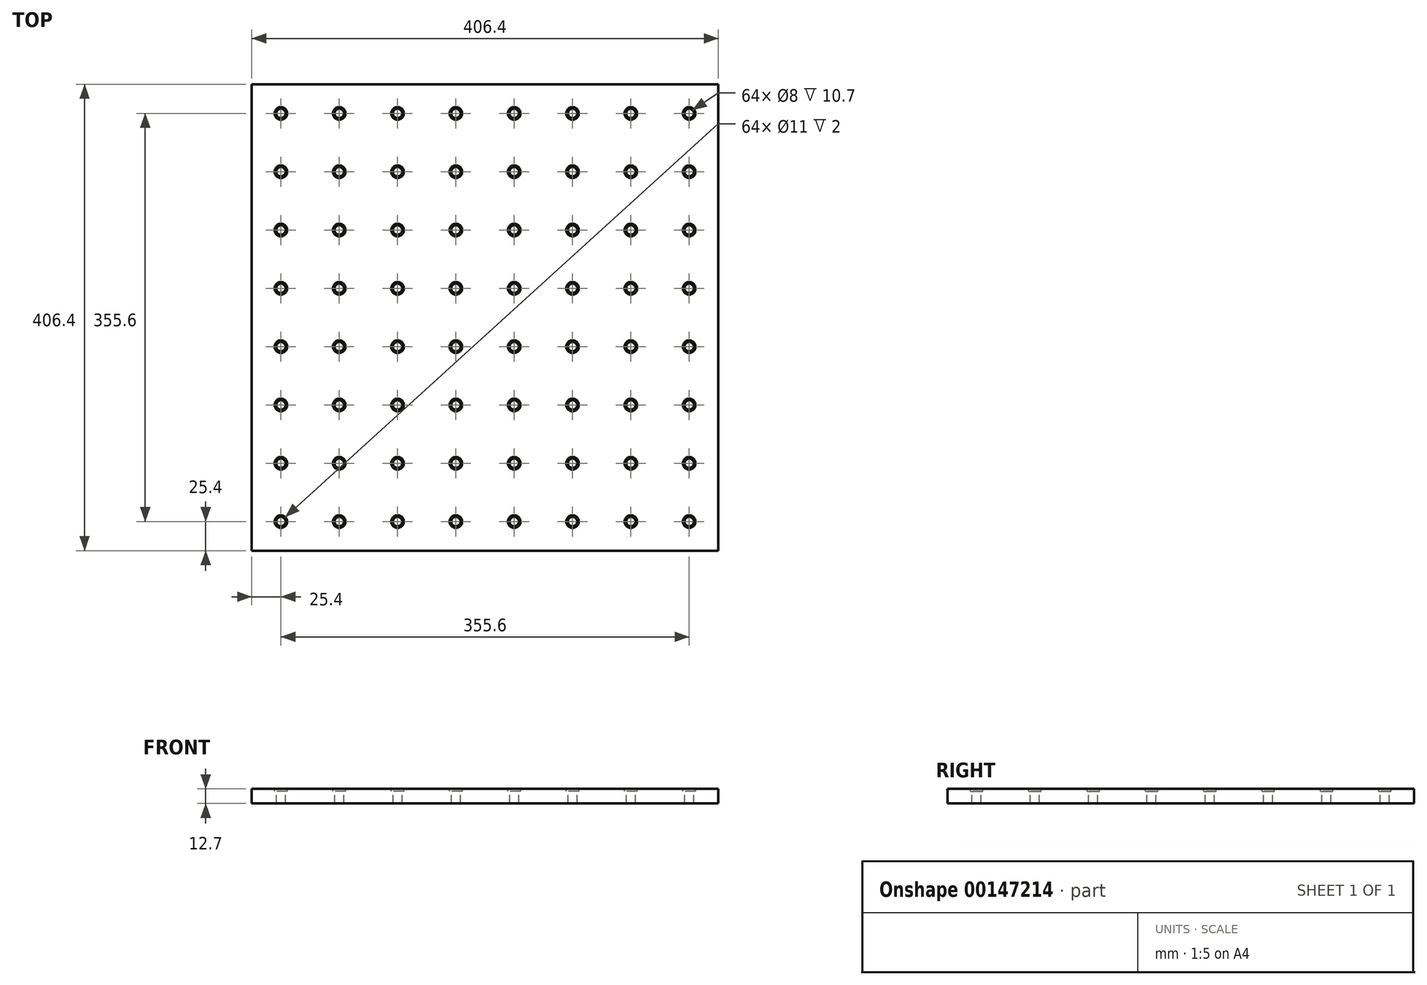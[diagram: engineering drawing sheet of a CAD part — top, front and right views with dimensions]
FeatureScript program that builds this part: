
annotation { "Feature Type Name" : "Feature", "Feature Type Description" : "" }
export const myFeature = defineFeature(function(context is Context, id is Id, definition is map)
    precondition{}
    {
        {
            var Q0;
            Q0=qCreatedBy(makeId("Top.planeOp"),FACE);
            var sketch = newSketch(context, id + "F0", { "sketchPlane" : qUnion([Q0])});
            skLineSegment(sketch, "E0.bottom", {"start": v(0, 0) * mm, "end": v(406.4, 0) * mm});
            skLineSegment(sketch, "E0.top", {"start": v(0, -406.4) * mm, "end": v(406.4, -406.4) * mm});
            skLineSegment(sketch, "E0.left", {"start": v(0, 0) * mm, "end": v(0, -406.4) * mm});
            skLineSegment(sketch, "E0.right", {"start": v(406.4, 0) * mm, "end": v(406.4, -406.4) * mm});
            skLineSegment(sketch, "E1", {"start": v(25.4, 5.4) * mm, "end": v(25.4, -53.58) * mm, "construction": true});
            skLineSegment(sketch, "E2", {"start": v(-10.34, -25.4) * mm, "end": v(59.96, -25.4) * mm, "construction": true});
            skCircle(sketch, "E3", {"center": v(25.4, -25.4) * mm, "radius": 4 * mm});
            skCircle(sketch, "E4", {"center": v(25.4, -25.4) * mm, "radius": 5.5 * mm});
            skCircle(sketch, "E5.0.1.0", {"center": v(25.4, -76.2) * mm, "radius": 5.5 * mm});
            skCircle(sketch, "E5.0.1.1", {"center": v(25.4, -76.2) * mm, "radius": 4 * mm});
            skCircle(sketch, "E5.0.2.0", {"center": v(25.4, -127) * mm, "radius": 5.5 * mm});
            skCircle(sketch, "E5.0.2.1", {"center": v(25.4, -127) * mm, "radius": 4 * mm});
            skCircle(sketch, "E5.0.3.0", {"center": v(25.4, -177.8) * mm, "radius": 5.5 * mm});
            skCircle(sketch, "E5.0.3.1", {"center": v(25.4, -177.8) * mm, "radius": 4 * mm});
            skCircle(sketch, "E5.0.4.0", {"center": v(25.4, -228.6) * mm, "radius": 5.5 * mm});
            skCircle(sketch, "E5.0.4.1", {"center": v(25.4, -228.6) * mm, "radius": 4 * mm});
            skCircle(sketch, "E5.0.5.0", {"center": v(25.4, -279.4) * mm, "radius": 5.5 * mm});
            skCircle(sketch, "E5.0.5.1", {"center": v(25.4, -279.4) * mm, "radius": 4 * mm});
            skCircle(sketch, "E5.0.6.0", {"center": v(25.4, -330.2) * mm, "radius": 5.5 * mm});
            skCircle(sketch, "E5.0.6.1", {"center": v(25.4, -330.2) * mm, "radius": 4 * mm});
            skCircle(sketch, "E5.0.7.0", {"center": v(25.4, -381) * mm, "radius": 5.5 * mm});
            skCircle(sketch, "E5.0.7.1", {"center": v(25.4, -381) * mm, "radius": 4 * mm});
            skCircle(sketch, "E5.1.0.0", {"center": v(76.2, -25.4) * mm, "radius": 5.5 * mm});
            skCircle(sketch, "E5.1.0.1", {"center": v(76.2, -25.4) * mm, "radius": 4 * mm});
            skCircle(sketch, "E5.1.1.0", {"center": v(76.2, -76.2) * mm, "radius": 5.5 * mm});
            skCircle(sketch, "E5.1.1.1", {"center": v(76.2, -76.2) * mm, "radius": 4 * mm});
            skCircle(sketch, "E5.1.2.0", {"center": v(76.2, -127) * mm, "radius": 5.5 * mm});
            skCircle(sketch, "E5.1.2.1", {"center": v(76.2, -127) * mm, "radius": 4 * mm});
            skCircle(sketch, "E5.1.3.0", {"center": v(76.2, -177.8) * mm, "radius": 5.5 * mm});
            skCircle(sketch, "E5.1.3.1", {"center": v(76.2, -177.8) * mm, "radius": 4 * mm});
            skCircle(sketch, "E5.1.4.0", {"center": v(76.2, -228.6) * mm, "radius": 5.5 * mm});
            skCircle(sketch, "E5.1.4.1", {"center": v(76.2, -228.6) * mm, "radius": 4 * mm});
            skCircle(sketch, "E5.1.5.0", {"center": v(76.2, -279.4) * mm, "radius": 5.5 * mm});
            skCircle(sketch, "E5.1.5.1", {"center": v(76.2, -279.4) * mm, "radius": 4 * mm});
            skCircle(sketch, "E5.1.6.0", {"center": v(76.2, -330.2) * mm, "radius": 5.5 * mm});
            skCircle(sketch, "E5.1.6.1", {"center": v(76.2, -330.2) * mm, "radius": 4 * mm});
            skCircle(sketch, "E5.1.7.0", {"center": v(76.2, -381) * mm, "radius": 5.5 * mm});
            skCircle(sketch, "E5.1.7.1", {"center": v(76.2, -381) * mm, "radius": 4 * mm});
            skCircle(sketch, "E5.2.0.0", {"center": v(127, -25.4) * mm, "radius": 5.5 * mm});
            skCircle(sketch, "E5.2.0.1", {"center": v(127, -25.4) * mm, "radius": 4 * mm});
            skCircle(sketch, "E5.2.1.0", {"center": v(127, -76.2) * mm, "radius": 5.5 * mm});
            skCircle(sketch, "E5.2.1.1", {"center": v(127, -76.2) * mm, "radius": 4 * mm});
            skCircle(sketch, "E5.2.2.0", {"center": v(127, -127) * mm, "radius": 5.5 * mm});
            skCircle(sketch, "E5.2.2.1", {"center": v(127, -127) * mm, "radius": 4 * mm});
            skCircle(sketch, "E5.2.3.0", {"center": v(127, -177.8) * mm, "radius": 5.5 * mm});
            skCircle(sketch, "E5.2.3.1", {"center": v(127, -177.8) * mm, "radius": 4 * mm});
            skCircle(sketch, "E5.2.4.0", {"center": v(127, -228.6) * mm, "radius": 5.5 * mm});
            skCircle(sketch, "E5.2.4.1", {"center": v(127, -228.6) * mm, "radius": 4 * mm});
            skCircle(sketch, "E5.2.5.0", {"center": v(127, -279.4) * mm, "radius": 5.5 * mm});
            skCircle(sketch, "E5.2.5.1", {"center": v(127, -279.4) * mm, "radius": 4 * mm});
            skCircle(sketch, "E5.2.6.0", {"center": v(127, -330.2) * mm, "radius": 5.5 * mm});
            skCircle(sketch, "E5.2.6.1", {"center": v(127, -330.2) * mm, "radius": 4 * mm});
            skCircle(sketch, "E5.2.7.0", {"center": v(127, -381) * mm, "radius": 5.5 * mm});
            skCircle(sketch, "E5.2.7.1", {"center": v(127, -381) * mm, "radius": 4 * mm});
            skCircle(sketch, "E5.3.0.0", {"center": v(177.8, -25.4) * mm, "radius": 5.5 * mm});
            skCircle(sketch, "E5.3.0.1", {"center": v(177.8, -25.4) * mm, "radius": 4 * mm});
            skCircle(sketch, "E5.3.1.0", {"center": v(177.8, -76.2) * mm, "radius": 5.5 * mm});
            skCircle(sketch, "E5.3.1.1", {"center": v(177.8, -76.2) * mm, "radius": 4 * mm});
            skCircle(sketch, "E5.3.2.0", {"center": v(177.8, -127) * mm, "radius": 5.5 * mm});
            skCircle(sketch, "E5.3.2.1", {"center": v(177.8, -127) * mm, "radius": 4 * mm});
            skCircle(sketch, "E5.3.3.0", {"center": v(177.8, -177.8) * mm, "radius": 5.5 * mm});
            skCircle(sketch, "E5.3.3.1", {"center": v(177.8, -177.8) * mm, "radius": 4 * mm});
            skCircle(sketch, "E5.3.4.0", {"center": v(177.8, -228.6) * mm, "radius": 5.5 * mm});
            skCircle(sketch, "E5.3.4.1", {"center": v(177.8, -228.6) * mm, "radius": 4 * mm});
            skCircle(sketch, "E5.3.5.0", {"center": v(177.8, -279.4) * mm, "radius": 5.5 * mm});
            skCircle(sketch, "E5.3.5.1", {"center": v(177.8, -279.4) * mm, "radius": 4 * mm});
            skCircle(sketch, "E5.3.6.0", {"center": v(177.8, -330.2) * mm, "radius": 5.5 * mm});
            skCircle(sketch, "E5.3.6.1", {"center": v(177.8, -330.2) * mm, "radius": 4 * mm});
            skCircle(sketch, "E5.3.7.0", {"center": v(177.8, -381) * mm, "radius": 5.5 * mm});
            skCircle(sketch, "E5.3.7.1", {"center": v(177.8, -381) * mm, "radius": 4 * mm});
            skCircle(sketch, "E5.4.0.0", {"center": v(228.6, -25.4) * mm, "radius": 5.5 * mm});
            skCircle(sketch, "E5.4.0.1", {"center": v(228.6, -25.4) * mm, "radius": 4 * mm});
            skCircle(sketch, "E5.4.1.0", {"center": v(228.6, -76.2) * mm, "radius": 5.5 * mm});
            skCircle(sketch, "E5.4.1.1", {"center": v(228.6, -76.2) * mm, "radius": 4 * mm});
            skCircle(sketch, "E5.4.2.0", {"center": v(228.6, -127) * mm, "radius": 5.5 * mm});
            skCircle(sketch, "E5.4.2.1", {"center": v(228.6, -127) * mm, "radius": 4 * mm});
            skCircle(sketch, "E5.4.3.0", {"center": v(228.6, -177.8) * mm, "radius": 5.5 * mm});
            skCircle(sketch, "E5.4.3.1", {"center": v(228.6, -177.8) * mm, "radius": 4 * mm});
            skCircle(sketch, "E5.4.4.0", {"center": v(228.6, -228.6) * mm, "radius": 5.5 * mm});
            skCircle(sketch, "E5.4.4.1", {"center": v(228.6, -228.6) * mm, "radius": 4 * mm});
            skCircle(sketch, "E5.4.5.0", {"center": v(228.6, -279.4) * mm, "radius": 5.5 * mm});
            skCircle(sketch, "E5.4.5.1", {"center": v(228.6, -279.4) * mm, "radius": 4 * mm});
            skCircle(sketch, "E5.4.6.0", {"center": v(228.6, -330.2) * mm, "radius": 5.5 * mm});
            skCircle(sketch, "E5.4.6.1", {"center": v(228.6, -330.2) * mm, "radius": 4 * mm});
            skCircle(sketch, "E5.4.7.0", {"center": v(228.6, -381) * mm, "radius": 5.5 * mm});
            skCircle(sketch, "E5.4.7.1", {"center": v(228.6, -381) * mm, "radius": 4 * mm});
            skCircle(sketch, "E5.5.0.0", {"center": v(279.4, -25.4) * mm, "radius": 5.5 * mm});
            skCircle(sketch, "E5.5.0.1", {"center": v(279.4, -25.4) * mm, "radius": 4 * mm});
            skCircle(sketch, "E5.5.1.0", {"center": v(279.4, -76.2) * mm, "radius": 5.5 * mm});
            skCircle(sketch, "E5.5.1.1", {"center": v(279.4, -76.2) * mm, "radius": 4 * mm});
            skCircle(sketch, "E5.5.2.0", {"center": v(279.4, -127) * mm, "radius": 5.5 * mm});
            skCircle(sketch, "E5.5.2.1", {"center": v(279.4, -127) * mm, "radius": 4 * mm});
            skCircle(sketch, "E5.5.3.0", {"center": v(279.4, -177.8) * mm, "radius": 5.5 * mm});
            skCircle(sketch, "E5.5.3.1", {"center": v(279.4, -177.8) * mm, "radius": 4 * mm});
            skCircle(sketch, "E5.5.4.0", {"center": v(279.4, -228.6) * mm, "radius": 5.5 * mm});
            skCircle(sketch, "E5.5.4.1", {"center": v(279.4, -228.6) * mm, "radius": 4 * mm});
            skCircle(sketch, "E5.5.5.0", {"center": v(279.4, -279.4) * mm, "radius": 5.5 * mm});
            skCircle(sketch, "E5.5.5.1", {"center": v(279.4, -279.4) * mm, "radius": 4 * mm});
            skCircle(sketch, "E5.5.6.0", {"center": v(279.4, -330.2) * mm, "radius": 5.5 * mm});
            skCircle(sketch, "E5.5.6.1", {"center": v(279.4, -330.2) * mm, "radius": 4 * mm});
            skCircle(sketch, "E5.5.7.0", {"center": v(279.4, -381) * mm, "radius": 5.5 * mm});
            skCircle(sketch, "E5.5.7.1", {"center": v(279.4, -381) * mm, "radius": 4 * mm});
            skCircle(sketch, "E5.6.0.0", {"center": v(330.2, -25.4) * mm, "radius": 5.5 * mm});
            skCircle(sketch, "E5.6.0.1", {"center": v(330.2, -25.4) * mm, "radius": 4 * mm});
            skCircle(sketch, "E5.6.1.0", {"center": v(330.2, -76.2) * mm, "radius": 5.5 * mm});
            skCircle(sketch, "E5.6.1.1", {"center": v(330.2, -76.2) * mm, "radius": 4 * mm});
            skCircle(sketch, "E5.6.2.0", {"center": v(330.2, -127) * mm, "radius": 5.5 * mm});
            skCircle(sketch, "E5.6.2.1", {"center": v(330.2, -127) * mm, "radius": 4 * mm});
            skCircle(sketch, "E5.6.3.0", {"center": v(330.2, -177.8) * mm, "radius": 5.5 * mm});
            skCircle(sketch, "E5.6.3.1", {"center": v(330.2, -177.8) * mm, "radius": 4 * mm});
            skCircle(sketch, "E5.6.4.0", {"center": v(330.2, -228.6) * mm, "radius": 5.5 * mm});
            skCircle(sketch, "E5.6.4.1", {"center": v(330.2, -228.6) * mm, "radius": 4 * mm});
            skCircle(sketch, "E5.6.5.0", {"center": v(330.2, -279.4) * mm, "radius": 5.5 * mm});
            skCircle(sketch, "E5.6.5.1", {"center": v(330.2, -279.4) * mm, "radius": 4 * mm});
            skCircle(sketch, "E5.6.6.0", {"center": v(330.2, -330.2) * mm, "radius": 5.5 * mm});
            skCircle(sketch, "E5.6.6.1", {"center": v(330.2, -330.2) * mm, "radius": 4 * mm});
            skCircle(sketch, "E5.6.7.0", {"center": v(330.2, -381) * mm, "radius": 5.5 * mm});
            skCircle(sketch, "E5.6.7.1", {"center": v(330.2, -381) * mm, "radius": 4 * mm});
            skCircle(sketch, "E5.7.0.0", {"center": v(381, -25.4) * mm, "radius": 5.5 * mm});
            skCircle(sketch, "E5.7.0.1", {"center": v(381, -25.4) * mm, "radius": 4 * mm});
            skCircle(sketch, "E5.7.1.0", {"center": v(381, -76.2) * mm, "radius": 5.5 * mm});
            skCircle(sketch, "E5.7.1.1", {"center": v(381, -76.2) * mm, "radius": 4 * mm});
            skCircle(sketch, "E5.7.2.0", {"center": v(381, -127) * mm, "radius": 5.5 * mm});
            skCircle(sketch, "E5.7.2.1", {"center": v(381, -127) * mm, "radius": 4 * mm});
            skCircle(sketch, "E5.7.3.0", {"center": v(381, -177.8) * mm, "radius": 5.5 * mm});
            skCircle(sketch, "E5.7.3.1", {"center": v(381, -177.8) * mm, "radius": 4 * mm});
            skCircle(sketch, "E5.7.4.0", {"center": v(381, -228.6) * mm, "radius": 5.5 * mm});
            skCircle(sketch, "E5.7.4.1", {"center": v(381, -228.6) * mm, "radius": 4 * mm});
            skCircle(sketch, "E5.7.5.0", {"center": v(381, -279.4) * mm, "radius": 5.5 * mm});
            skCircle(sketch, "E5.7.5.1", {"center": v(381, -279.4) * mm, "radius": 4 * mm});
            skCircle(sketch, "E5.7.6.0", {"center": v(381, -330.2) * mm, "radius": 5.5 * mm});
            skCircle(sketch, "E5.7.6.1", {"center": v(381, -330.2) * mm, "radius": 4 * mm});
            skCircle(sketch, "E5.7.7.0", {"center": v(381, -381) * mm, "radius": 5.5 * mm});
            skCircle(sketch, "E5.7.7.1", {"center": v(381, -381) * mm, "radius": 4 * mm});
            skLineSegment(sketch, "E5.direction1", {"start": v(25.4, -25.4) * mm, "end": v(76.2, -25.4) * mm, "construction": true});
            skLineSegment(sketch, "E5.direction2", {"start": v(25.4, -25.4) * mm, "end": v(25.4, -76.2) * mm, "construction": true});
            skSolve(sketch);
        }
        {
            var Q0;
            Q0 = qSketchRegion(id + "F0", true);
            var Q1;
            Q1=makeQuery(id+"F0.imprint","IMPRINT",FACE,{"disambiguationData":[TD([[makeQuery(id+"F0.imprint","IMPRINT",EDGE,{"derivedFrom":sQuery(id+"F0.wireOp",EDGE,"E3")}),-1.0]])]});
            var Q2;
            Q2=makeQuery(id+"F0.imprint","IMPRINT",FACE,{"disambiguationData":[TD([[makeQuery(id+"F0.imprint","IMPRINT",EDGE,{"derivedFrom":sQuery(id+"F0.wireOp",EDGE,"E5.1.0.0")}),1.0]])]});
            var Q3;
            Q3=makeQuery(id+"F0.imprint","IMPRINT",FACE,{"disambiguationData":[TD([[makeQuery(id+"F0.imprint","IMPRINT",EDGE,{"derivedFrom":sQuery(id+"F0.wireOp",EDGE,"E5.2.0.0")}),1.0]])]});
            var Q4;
            Q4=makeQuery(id+"F0.imprint","IMPRINT",FACE,{"disambiguationData":[TD([[makeQuery(id+"F0.imprint","IMPRINT",EDGE,{"derivedFrom":sQuery(id+"F0.wireOp",EDGE,"E5.3.0.0")}),1.0]])]});
            var Q5;
            Q5=makeQuery(id+"F0.imprint","IMPRINT",FACE,{"disambiguationData":[TD([[makeQuery(id+"F0.imprint","IMPRINT",EDGE,{"derivedFrom":sQuery(id+"F0.wireOp",EDGE,"E5.4.0.0")}),1.0]])]});
            var Q6;
            Q6=makeQuery(id+"F0.imprint","IMPRINT",FACE,{"disambiguationData":[TD([[makeQuery(id+"F0.imprint","IMPRINT",EDGE,{"derivedFrom":sQuery(id+"F0.wireOp",EDGE,"E5.5.0.0")}),1.0]])]});
            var Q7;
            Q7=makeQuery(id+"F0.imprint","IMPRINT",FACE,{"disambiguationData":[TD([[makeQuery(id+"F0.imprint","IMPRINT",EDGE,{"derivedFrom":sQuery(id+"F0.wireOp",EDGE,"E5.6.0.0")}),1.0]])]});
            var Q8;
            Q8=makeQuery(id+"F0.imprint","IMPRINT",FACE,{"disambiguationData":[TD([[makeQuery(id+"F0.imprint","IMPRINT",EDGE,{"derivedFrom":sQuery(id+"F0.wireOp",EDGE,"E5.7.0.0")}),1.0]])]});
            var Q9;
            Q9=makeQuery(id+"F0.imprint","IMPRINT",FACE,{"disambiguationData":[TD([[makeQuery(id+"F0.imprint","IMPRINT",EDGE,{"derivedFrom":sQuery(id+"F0.wireOp",EDGE,"E5.0.1.0")}),1.0]])]});
            var Q10;
            Q10=makeQuery(id+"F0.imprint","IMPRINT",FACE,{"disambiguationData":[TD([[makeQuery(id+"F0.imprint","IMPRINT",EDGE,{"derivedFrom":sQuery(id+"F0.wireOp",EDGE,"E5.1.1.0")}),1.0]])]});
            var Q11;
            Q11=makeQuery(id+"F0.imprint","IMPRINT",FACE,{"disambiguationData":[TD([[makeQuery(id+"F0.imprint","IMPRINT",EDGE,{"derivedFrom":sQuery(id+"F0.wireOp",EDGE,"E5.2.1.0")}),1.0]])]});
            var Q12;
            Q12=makeQuery(id+"F0.imprint","IMPRINT",FACE,{"disambiguationData":[TD([[makeQuery(id+"F0.imprint","IMPRINT",EDGE,{"derivedFrom":sQuery(id+"F0.wireOp",EDGE,"E5.3.1.0")}),1.0]])]});
            var Q13;
            Q13=makeQuery(id+"F0.imprint","IMPRINT",FACE,{"disambiguationData":[TD([[makeQuery(id+"F0.imprint","IMPRINT",EDGE,{"derivedFrom":sQuery(id+"F0.wireOp",EDGE,"E5.4.1.0")}),1.0]])]});
            var Q14;
            Q14=makeQuery(id+"F0.imprint","IMPRINT",FACE,{"disambiguationData":[TD([[makeQuery(id+"F0.imprint","IMPRINT",EDGE,{"derivedFrom":sQuery(id+"F0.wireOp",EDGE,"E5.5.1.0")}),1.0]])]});
            var Q15;
            Q15=makeQuery(id+"F0.imprint","IMPRINT",FACE,{"disambiguationData":[TD([[makeQuery(id+"F0.imprint","IMPRINT",EDGE,{"derivedFrom":sQuery(id+"F0.wireOp",EDGE,"E5.6.1.0")}),1.0]])]});
            var Q16;
            Q16=makeQuery(id+"F0.imprint","IMPRINT",FACE,{"disambiguationData":[TD([[makeQuery(id+"F0.imprint","IMPRINT",EDGE,{"derivedFrom":sQuery(id+"F0.wireOp",EDGE,"E5.7.1.0")}),1.0]])]});
            var Q17;
            Q17=makeQuery(id+"F0.imprint","IMPRINT",FACE,{"disambiguationData":[TD([[makeQuery(id+"F0.imprint","IMPRINT",EDGE,{"derivedFrom":sQuery(id+"F0.wireOp",EDGE,"E5.7.2.0")}),1.0]])]});
            var Q18;
            Q18=makeQuery(id+"F0.imprint","IMPRINT",FACE,{"disambiguationData":[TD([[makeQuery(id+"F0.imprint","IMPRINT",EDGE,{"derivedFrom":sQuery(id+"F0.wireOp",EDGE,"E5.6.2.0")}),1.0]])]});
            var Q19;
            Q19=makeQuery(id+"F0.imprint","IMPRINT",FACE,{"disambiguationData":[TD([[makeQuery(id+"F0.imprint","IMPRINT",EDGE,{"derivedFrom":sQuery(id+"F0.wireOp",EDGE,"E5.5.2.0")}),1.0]])]});
            var Q20;
            Q20=makeQuery(id+"F0.imprint","IMPRINT",FACE,{"disambiguationData":[TD([[makeQuery(id+"F0.imprint","IMPRINT",EDGE,{"derivedFrom":sQuery(id+"F0.wireOp",EDGE,"E5.4.2.0")}),1.0]])]});
            var Q21;
            Q21=makeQuery(id+"F0.imprint","IMPRINT",FACE,{"disambiguationData":[TD([[makeQuery(id+"F0.imprint","IMPRINT",EDGE,{"derivedFrom":sQuery(id+"F0.wireOp",EDGE,"E5.3.2.0")}),1.0]])]});
            var Q22;
            Q22=makeQuery(id+"F0.imprint","IMPRINT",FACE,{"disambiguationData":[TD([[makeQuery(id+"F0.imprint","IMPRINT",EDGE,{"derivedFrom":sQuery(id+"F0.wireOp",EDGE,"E5.2.2.0")}),1.0]])]});
            var Q23;
            Q23=makeQuery(id+"F0.imprint","IMPRINT",FACE,{"disambiguationData":[TD([[makeQuery(id+"F0.imprint","IMPRINT",EDGE,{"derivedFrom":sQuery(id+"F0.wireOp",EDGE,"E5.1.2.0")}),1.0]])]});
            var Q24;
            Q24=makeQuery(id+"F0.imprint","IMPRINT",FACE,{"disambiguationData":[TD([[makeQuery(id+"F0.imprint","IMPRINT",EDGE,{"derivedFrom":sQuery(id+"F0.wireOp",EDGE,"E5.0.2.0")}),1.0]])]});
            var Q25;
            Q25=makeQuery(id+"F0.imprint","IMPRINT",FACE,{"disambiguationData":[TD([[makeQuery(id+"F0.imprint","IMPRINT",EDGE,{"derivedFrom":sQuery(id+"F0.wireOp",EDGE,"E5.0.3.0")}),1.0]])]});
            var Q26;
            Q26=makeQuery(id+"F0.imprint","IMPRINT",FACE,{"disambiguationData":[TD([[makeQuery(id+"F0.imprint","IMPRINT",EDGE,{"derivedFrom":sQuery(id+"F0.wireOp",EDGE,"E5.1.3.0")}),1.0]])]});
            var Q27;
            Q27=makeQuery(id+"F0.imprint","IMPRINT",FACE,{"disambiguationData":[TD([[makeQuery(id+"F0.imprint","IMPRINT",EDGE,{"derivedFrom":sQuery(id+"F0.wireOp",EDGE,"E5.2.3.0")}),1.0]])]});
            var Q28;
            Q28=makeQuery(id+"F0.imprint","IMPRINT",FACE,{"disambiguationData":[TD([[makeQuery(id+"F0.imprint","IMPRINT",EDGE,{"derivedFrom":sQuery(id+"F0.wireOp",EDGE,"E5.3.3.0")}),1.0]])]});
            var Q29;
            Q29=makeQuery(id+"F0.imprint","IMPRINT",FACE,{"disambiguationData":[TD([[makeQuery(id+"F0.imprint","IMPRINT",EDGE,{"derivedFrom":sQuery(id+"F0.wireOp",EDGE,"E5.4.3.0")}),1.0]])]});
            var Q30;
            Q30=makeQuery(id+"F0.imprint","IMPRINT",FACE,{"disambiguationData":[TD([[makeQuery(id+"F0.imprint","IMPRINT",EDGE,{"derivedFrom":sQuery(id+"F0.wireOp",EDGE,"E5.5.3.0")}),1.0]])]});
            var Q31;
            Q31=makeQuery(id+"F0.imprint","IMPRINT",FACE,{"disambiguationData":[TD([[makeQuery(id+"F0.imprint","IMPRINT",EDGE,{"derivedFrom":sQuery(id+"F0.wireOp",EDGE,"E5.6.3.0")}),1.0]])]});
            var Q32;
            Q32=makeQuery(id+"F0.imprint","IMPRINT",FACE,{"disambiguationData":[TD([[makeQuery(id+"F0.imprint","IMPRINT",EDGE,{"derivedFrom":sQuery(id+"F0.wireOp",EDGE,"E5.7.3.0")}),1.0]])]});
            var Q33;
            Q33=makeQuery(id+"F0.imprint","IMPRINT",FACE,{"disambiguationData":[TD([[makeQuery(id+"F0.imprint","IMPRINT",EDGE,{"derivedFrom":sQuery(id+"F0.wireOp",EDGE,"E5.7.4.0")}),1.0]])]});
            var Q34;
            Q34=makeQuery(id+"F0.imprint","IMPRINT",FACE,{"disambiguationData":[TD([[makeQuery(id+"F0.imprint","IMPRINT",EDGE,{"derivedFrom":sQuery(id+"F0.wireOp",EDGE,"E5.6.4.0")}),1.0]])]});
            var Q35;
            Q35=makeQuery(id+"F0.imprint","IMPRINT",FACE,{"disambiguationData":[TD([[makeQuery(id+"F0.imprint","IMPRINT",EDGE,{"derivedFrom":sQuery(id+"F0.wireOp",EDGE,"E5.5.4.0")}),1.0]])]});
            var Q36;
            Q36=makeQuery(id+"F0.imprint","IMPRINT",FACE,{"disambiguationData":[TD([[makeQuery(id+"F0.imprint","IMPRINT",EDGE,{"derivedFrom":sQuery(id+"F0.wireOp",EDGE,"E5.4.4.0")}),1.0]])]});
            var Q37;
            Q37=makeQuery(id+"F0.imprint","IMPRINT",FACE,{"disambiguationData":[TD([[makeQuery(id+"F0.imprint","IMPRINT",EDGE,{"derivedFrom":sQuery(id+"F0.wireOp",EDGE,"E5.3.4.0")}),1.0]])]});
            var Q38;
            Q38=makeQuery(id+"F0.imprint","IMPRINT",FACE,{"disambiguationData":[TD([[makeQuery(id+"F0.imprint","IMPRINT",EDGE,{"derivedFrom":sQuery(id+"F0.wireOp",EDGE,"E5.2.4.0")}),1.0]])]});
            var Q39;
            Q39=makeQuery(id+"F0.imprint","IMPRINT",FACE,{"disambiguationData":[TD([[makeQuery(id+"F0.imprint","IMPRINT",EDGE,{"derivedFrom":sQuery(id+"F0.wireOp",EDGE,"E5.1.4.0")}),1.0]])]});
            var Q40;
            Q40=makeQuery(id+"F0.imprint","IMPRINT",FACE,{"disambiguationData":[TD([[makeQuery(id+"F0.imprint","IMPRINT",EDGE,{"derivedFrom":sQuery(id+"F0.wireOp",EDGE,"E5.0.4.0")}),1.0]])]});
            var Q41;
            Q41=makeQuery(id+"F0.imprint","IMPRINT",FACE,{"disambiguationData":[TD([[makeQuery(id+"F0.imprint","IMPRINT",EDGE,{"derivedFrom":sQuery(id+"F0.wireOp",EDGE,"E5.0.5.0")}),1.0]])]});
            var Q42;
            Q42=makeQuery(id+"F0.imprint","IMPRINT",FACE,{"disambiguationData":[TD([[makeQuery(id+"F0.imprint","IMPRINT",EDGE,{"derivedFrom":sQuery(id+"F0.wireOp",EDGE,"E5.1.5.0")}),1.0]])]});
            var Q43;
            Q43=makeQuery(id+"F0.imprint","IMPRINT",FACE,{"disambiguationData":[TD([[makeQuery(id+"F0.imprint","IMPRINT",EDGE,{"derivedFrom":sQuery(id+"F0.wireOp",EDGE,"E5.2.5.0")}),1.0]])]});
            var Q44;
            Q44=makeQuery(id+"F0.imprint","IMPRINT",FACE,{"disambiguationData":[TD([[makeQuery(id+"F0.imprint","IMPRINT",EDGE,{"derivedFrom":sQuery(id+"F0.wireOp",EDGE,"E5.3.5.0")}),1.0]])]});
            var Q45;
            Q45=makeQuery(id+"F0.imprint","IMPRINT",FACE,{"disambiguationData":[TD([[makeQuery(id+"F0.imprint","IMPRINT",EDGE,{"derivedFrom":sQuery(id+"F0.wireOp",EDGE,"E5.4.5.0")}),1.0]])]});
            var Q46;
            Q46=makeQuery(id+"F0.imprint","IMPRINT",FACE,{"disambiguationData":[TD([[makeQuery(id+"F0.imprint","IMPRINT",EDGE,{"derivedFrom":sQuery(id+"F0.wireOp",EDGE,"E5.5.5.0")}),1.0]])]});
            var Q47;
            Q47=makeQuery(id+"F0.imprint","IMPRINT",FACE,{"disambiguationData":[TD([[makeQuery(id+"F0.imprint","IMPRINT",EDGE,{"derivedFrom":sQuery(id+"F0.wireOp",EDGE,"E5.6.5.0")}),1.0]])]});
            var Q48;
            Q48=makeQuery(id+"F0.imprint","IMPRINT",FACE,{"disambiguationData":[TD([[makeQuery(id+"F0.imprint","IMPRINT",EDGE,{"derivedFrom":sQuery(id+"F0.wireOp",EDGE,"E5.7.5.0")}),1.0]])]});
            var Q49;
            Q49=makeQuery(id+"F0.imprint","IMPRINT",FACE,{"disambiguationData":[TD([[makeQuery(id+"F0.imprint","IMPRINT",EDGE,{"derivedFrom":sQuery(id+"F0.wireOp",EDGE,"E5.7.6.0")}),1.0]])]});
            var Q50;
            Q50=makeQuery(id+"F0.imprint","IMPRINT",FACE,{"disambiguationData":[TD([[makeQuery(id+"F0.imprint","IMPRINT",EDGE,{"derivedFrom":sQuery(id+"F0.wireOp",EDGE,"E5.6.6.0")}),1.0]])]});
            var Q51;
            Q51=makeQuery(id+"F0.imprint","IMPRINT",FACE,{"disambiguationData":[TD([[makeQuery(id+"F0.imprint","IMPRINT",EDGE,{"derivedFrom":sQuery(id+"F0.wireOp",EDGE,"E5.5.6.0")}),1.0]])]});
            var Q52;
            Q52=makeQuery(id+"F0.imprint","IMPRINT",FACE,{"disambiguationData":[TD([[makeQuery(id+"F0.imprint","IMPRINT",EDGE,{"derivedFrom":sQuery(id+"F0.wireOp",EDGE,"E5.4.6.0")}),1.0]])]});
            var Q53;
            Q53=makeQuery(id+"F0.imprint","IMPRINT",FACE,{"disambiguationData":[TD([[makeQuery(id+"F0.imprint","IMPRINT",EDGE,{"derivedFrom":sQuery(id+"F0.wireOp",EDGE,"E5.3.6.0")}),1.0]])]});
            var Q54;
            Q54=makeQuery(id+"F0.imprint","IMPRINT",FACE,{"disambiguationData":[TD([[makeQuery(id+"F0.imprint","IMPRINT",EDGE,{"derivedFrom":sQuery(id+"F0.wireOp",EDGE,"E5.2.6.0")}),1.0]])]});
            var Q55;
            Q55=makeQuery(id+"F0.imprint","IMPRINT",FACE,{"disambiguationData":[TD([[makeQuery(id+"F0.imprint","IMPRINT",EDGE,{"derivedFrom":sQuery(id+"F0.wireOp",EDGE,"E5.1.6.0")}),1.0]])]});
            var Q56;
            Q56=makeQuery(id+"F0.imprint","IMPRINT",FACE,{"disambiguationData":[TD([[makeQuery(id+"F0.imprint","IMPRINT",EDGE,{"derivedFrom":sQuery(id+"F0.wireOp",EDGE,"E5.0.6.0")}),1.0]])]});
            var Q57;
            Q57=makeQuery(id+"F0.imprint","IMPRINT",FACE,{"disambiguationData":[TD([[makeQuery(id+"F0.imprint","IMPRINT",EDGE,{"derivedFrom":sQuery(id+"F0.wireOp",EDGE,"E5.0.7.0")}),1.0]])]});
            var Q58;
            Q58=makeQuery(id+"F0.imprint","IMPRINT",FACE,{"disambiguationData":[TD([[makeQuery(id+"F0.imprint","IMPRINT",EDGE,{"derivedFrom":sQuery(id+"F0.wireOp",EDGE,"E5.1.7.0")}),1.0]])]});
            var Q59;
            Q59=makeQuery(id+"F0.imprint","IMPRINT",FACE,{"disambiguationData":[TD([[makeQuery(id+"F0.imprint","IMPRINT",EDGE,{"derivedFrom":sQuery(id+"F0.wireOp",EDGE,"E5.2.7.0")}),1.0]])]});
            var Q60;
            Q60=makeQuery(id+"F0.imprint","IMPRINT",FACE,{"disambiguationData":[TD([[makeQuery(id+"F0.imprint","IMPRINT",EDGE,{"derivedFrom":sQuery(id+"F0.wireOp",EDGE,"E5.3.7.0")}),1.0]])]});
            var Q61;
            Q61=makeQuery(id+"F0.imprint","IMPRINT",FACE,{"disambiguationData":[TD([[makeQuery(id+"F0.imprint","IMPRINT",EDGE,{"derivedFrom":sQuery(id+"F0.wireOp",EDGE,"E5.4.7.0")}),1.0]])]});
            var Q62;
            Q62=makeQuery(id+"F0.imprint","IMPRINT",FACE,{"disambiguationData":[TD([[makeQuery(id+"F0.imprint","IMPRINT",EDGE,{"derivedFrom":sQuery(id+"F0.wireOp",EDGE,"E5.5.7.0")}),1.0]])]});
            var Q63;
            Q63=makeQuery(id+"F0.imprint","IMPRINT",FACE,{"disambiguationData":[TD([[makeQuery(id+"F0.imprint","IMPRINT",EDGE,{"derivedFrom":sQuery(id+"F0.wireOp",EDGE,"E5.6.7.0")}),1.0]])]});
            var Q64;
            Q64=makeQuery(id+"F0.imprint","IMPRINT",FACE,{"disambiguationData":[TD([[makeQuery(id+"F0.imprint","IMPRINT",EDGE,{"derivedFrom":sQuery(id+"F0.wireOp",EDGE,"E5.7.7.0")}),1.0]])]});
            extrude(context, id + "F1", {"entities" : qUnion([Q0, Q1, Q2, Q3, Q4, Q5, Q6, Q7, Q8, Q9, Q10, Q11, Q12, Q13, Q14, Q15, Q16, Q17, Q18, Q19, Q20, Q21, Q22, Q23, Q24, Q25, Q26, Q27, Q28, Q29, Q30, Q31, Q32, Q33, Q34, Q35, Q36, Q37, Q38, Q39, Q40, Q41, Q42, Q43, Q44, Q45, Q46, Q47, Q48, Q49, Q50, Q51, Q52, Q53, Q54, Q55, Q56, Q57, Q58, Q59, Q60, Q61, Q62, Q63, Q64]), "oppositeDirection" : true, "depth" : 12.7 * mm});
        }
        {
            var Q0;
            Q0=makeQuery(id+"F0.imprint","IMPRINT",FACE,{"disambiguationData":[TD([[makeQuery(id+"F0.imprint","IMPRINT",EDGE,{"derivedFrom":sQuery(id+"F0.wireOp",EDGE,"E3")}),-1.0]])]});
            var Q1;
            Q1=makeQuery(id+"F0.imprint","IMPRINT",FACE,{"disambiguationData":[TD([[makeQuery(id+"F0.imprint","IMPRINT",EDGE,{"derivedFrom":sQuery(id+"F0.wireOp",EDGE,"E5.1.0.0")}),1.0]])]});
            var Q2;
            Q2=makeQuery(id+"F0.imprint","IMPRINT",FACE,{"disambiguationData":[TD([[makeQuery(id+"F0.imprint","IMPRINT",EDGE,{"derivedFrom":sQuery(id+"F0.wireOp",EDGE,"E5.2.0.0")}),1.0]])]});
            var Q3;
            Q3=makeQuery(id+"F0.imprint","IMPRINT",FACE,{"disambiguationData":[TD([[makeQuery(id+"F0.imprint","IMPRINT",EDGE,{"derivedFrom":sQuery(id+"F0.wireOp",EDGE,"E5.3.0.0")}),1.0]])]});
            var Q4;
            Q4=makeQuery(id+"F0.imprint","IMPRINT",FACE,{"disambiguationData":[TD([[makeQuery(id+"F0.imprint","IMPRINT",EDGE,{"derivedFrom":sQuery(id+"F0.wireOp",EDGE,"E5.4.0.0")}),1.0]])]});
            var Q5;
            Q5=makeQuery(id+"F0.imprint","IMPRINT",FACE,{"disambiguationData":[TD([[makeQuery(id+"F0.imprint","IMPRINT",EDGE,{"derivedFrom":sQuery(id+"F0.wireOp",EDGE,"E5.5.0.0")}),1.0]])]});
            var Q6;
            Q6=makeQuery(id+"F0.imprint","IMPRINT",FACE,{"disambiguationData":[TD([[makeQuery(id+"F0.imprint","IMPRINT",EDGE,{"derivedFrom":sQuery(id+"F0.wireOp",EDGE,"E5.6.0.0")}),1.0]])]});
            var Q7;
            Q7=makeQuery(id+"F0.imprint","IMPRINT",FACE,{"disambiguationData":[TD([[makeQuery(id+"F0.imprint","IMPRINT",EDGE,{"derivedFrom":sQuery(id+"F0.wireOp",EDGE,"E5.7.0.0")}),1.0]])]});
            var Q8;
            Q8=makeQuery(id+"F0.imprint","IMPRINT",FACE,{"disambiguationData":[TD([[makeQuery(id+"F0.imprint","IMPRINT",EDGE,{"derivedFrom":sQuery(id+"F0.wireOp",EDGE,"E5.7.1.0")}),1.0]])]});
            var Q9;
            Q9=makeQuery(id+"F0.imprint","IMPRINT",FACE,{"disambiguationData":[TD([[makeQuery(id+"F0.imprint","IMPRINT",EDGE,{"derivedFrom":sQuery(id+"F0.wireOp",EDGE,"E5.6.1.0")}),1.0]])]});
            var Q10;
            Q10=makeQuery(id+"F0.imprint","IMPRINT",FACE,{"disambiguationData":[TD([[makeQuery(id+"F0.imprint","IMPRINT",EDGE,{"derivedFrom":sQuery(id+"F0.wireOp",EDGE,"E5.5.1.0")}),1.0]])]});
            var Q11;
            Q11=makeQuery(id+"F0.imprint","IMPRINT",FACE,{"disambiguationData":[TD([[makeQuery(id+"F0.imprint","IMPRINT",EDGE,{"derivedFrom":sQuery(id+"F0.wireOp",EDGE,"E5.4.1.0")}),1.0]])]});
            var Q12;
            Q12=makeQuery(id+"F0.imprint","IMPRINT",FACE,{"disambiguationData":[TD([[makeQuery(id+"F0.imprint","IMPRINT",EDGE,{"derivedFrom":sQuery(id+"F0.wireOp",EDGE,"E5.3.1.0")}),1.0]])]});
            var Q13;
            Q13=makeQuery(id+"F0.imprint","IMPRINT",FACE,{"disambiguationData":[TD([[makeQuery(id+"F0.imprint","IMPRINT",EDGE,{"derivedFrom":sQuery(id+"F0.wireOp",EDGE,"E5.2.1.0")}),1.0]])]});
            var Q14;
            Q14=makeQuery(id+"F0.imprint","IMPRINT",FACE,{"disambiguationData":[TD([[makeQuery(id+"F0.imprint","IMPRINT",EDGE,{"derivedFrom":sQuery(id+"F0.wireOp",EDGE,"E5.1.1.0")}),1.0]])]});
            var Q15;
            Q15=makeQuery(id+"F0.imprint","IMPRINT",FACE,{"disambiguationData":[TD([[makeQuery(id+"F0.imprint","IMPRINT",EDGE,{"derivedFrom":sQuery(id+"F0.wireOp",EDGE,"E5.0.1.0")}),1.0]])]});
            var Q16;
            Q16=makeQuery(id+"F0.imprint","IMPRINT",FACE,{"disambiguationData":[TD([[makeQuery(id+"F0.imprint","IMPRINT",EDGE,{"derivedFrom":sQuery(id+"F0.wireOp",EDGE,"E5.0.2.0")}),1.0]])]});
            var Q17;
            Q17=makeQuery(id+"F0.imprint","IMPRINT",FACE,{"disambiguationData":[TD([[makeQuery(id+"F0.imprint","IMPRINT",EDGE,{"derivedFrom":sQuery(id+"F0.wireOp",EDGE,"E5.1.2.0")}),1.0]])]});
            var Q18;
            Q18=makeQuery(id+"F0.imprint","IMPRINT",FACE,{"disambiguationData":[TD([[makeQuery(id+"F0.imprint","IMPRINT",EDGE,{"derivedFrom":sQuery(id+"F0.wireOp",EDGE,"E5.2.2.0")}),1.0]])]});
            var Q19;
            Q19=makeQuery(id+"F0.imprint","IMPRINT",FACE,{"disambiguationData":[TD([[makeQuery(id+"F0.imprint","IMPRINT",EDGE,{"derivedFrom":sQuery(id+"F0.wireOp",EDGE,"E5.3.2.0")}),1.0]])]});
            var Q20;
            Q20=makeQuery(id+"F0.imprint","IMPRINT",FACE,{"disambiguationData":[TD([[makeQuery(id+"F0.imprint","IMPRINT",EDGE,{"derivedFrom":sQuery(id+"F0.wireOp",EDGE,"E5.4.2.0")}),1.0]])]});
            var Q21;
            Q21=makeQuery(id+"F0.imprint","IMPRINT",FACE,{"disambiguationData":[TD([[makeQuery(id+"F0.imprint","IMPRINT",EDGE,{"derivedFrom":sQuery(id+"F0.wireOp",EDGE,"E5.5.2.0")}),1.0]])]});
            var Q22;
            Q22=makeQuery(id+"F0.imprint","IMPRINT",FACE,{"disambiguationData":[TD([[makeQuery(id+"F0.imprint","IMPRINT",EDGE,{"derivedFrom":sQuery(id+"F0.wireOp",EDGE,"E5.6.2.0")}),1.0]])]});
            var Q23;
            Q23=makeQuery(id+"F0.imprint","IMPRINT",FACE,{"disambiguationData":[TD([[makeQuery(id+"F0.imprint","IMPRINT",EDGE,{"derivedFrom":sQuery(id+"F0.wireOp",EDGE,"E5.7.2.0")}),1.0]])]});
            var Q24;
            Q24=makeQuery(id+"F0.imprint","IMPRINT",FACE,{"disambiguationData":[TD([[makeQuery(id+"F0.imprint","IMPRINT",EDGE,{"derivedFrom":sQuery(id+"F0.wireOp",EDGE,"E5.7.3.0")}),1.0]])]});
            var Q25;
            Q25=makeQuery(id+"F0.imprint","IMPRINT",FACE,{"disambiguationData":[TD([[makeQuery(id+"F0.imprint","IMPRINT",EDGE,{"derivedFrom":sQuery(id+"F0.wireOp",EDGE,"E5.6.3.0")}),1.0]])]});
            var Q26;
            Q26=makeQuery(id+"F0.imprint","IMPRINT",FACE,{"disambiguationData":[TD([[makeQuery(id+"F0.imprint","IMPRINT",EDGE,{"derivedFrom":sQuery(id+"F0.wireOp",EDGE,"E5.5.3.0")}),1.0]])]});
            var Q27;
            Q27=makeQuery(id+"F0.imprint","IMPRINT",FACE,{"disambiguationData":[TD([[makeQuery(id+"F0.imprint","IMPRINT",EDGE,{"derivedFrom":sQuery(id+"F0.wireOp",EDGE,"E5.4.3.0")}),1.0]])]});
            var Q28;
            Q28=makeQuery(id+"F0.imprint","IMPRINT",FACE,{"disambiguationData":[TD([[makeQuery(id+"F0.imprint","IMPRINT",EDGE,{"derivedFrom":sQuery(id+"F0.wireOp",EDGE,"E5.3.3.0")}),1.0]])]});
            var Q29;
            Q29=makeQuery(id+"F0.imprint","IMPRINT",FACE,{"disambiguationData":[TD([[makeQuery(id+"F0.imprint","IMPRINT",EDGE,{"derivedFrom":sQuery(id+"F0.wireOp",EDGE,"E5.2.3.0")}),1.0]])]});
            var Q30;
            Q30=makeQuery(id+"F0.imprint","IMPRINT",FACE,{"disambiguationData":[TD([[makeQuery(id+"F0.imprint","IMPRINT",EDGE,{"derivedFrom":sQuery(id+"F0.wireOp",EDGE,"E5.1.3.0")}),1.0]])]});
            var Q31;
            Q31=makeQuery(id+"F0.imprint","IMPRINT",FACE,{"disambiguationData":[TD([[makeQuery(id+"F0.imprint","IMPRINT",EDGE,{"derivedFrom":sQuery(id+"F0.wireOp",EDGE,"E5.0.3.0")}),1.0]])]});
            var Q32;
            Q32=makeQuery(id+"F0.imprint","IMPRINT",FACE,{"disambiguationData":[TD([[makeQuery(id+"F0.imprint","IMPRINT",EDGE,{"derivedFrom":sQuery(id+"F0.wireOp",EDGE,"E5.0.4.0")}),1.0]])]});
            var Q33;
            Q33=makeQuery(id+"F0.imprint","IMPRINT",FACE,{"disambiguationData":[TD([[makeQuery(id+"F0.imprint","IMPRINT",EDGE,{"derivedFrom":sQuery(id+"F0.wireOp",EDGE,"E5.1.4.0")}),1.0]])]});
            var Q34;
            Q34=makeQuery(id+"F0.imprint","IMPRINT",FACE,{"disambiguationData":[TD([[makeQuery(id+"F0.imprint","IMPRINT",EDGE,{"derivedFrom":sQuery(id+"F0.wireOp",EDGE,"E5.2.4.0")}),1.0]])]});
            var Q35;
            Q35=makeQuery(id+"F0.imprint","IMPRINT",FACE,{"disambiguationData":[TD([[makeQuery(id+"F0.imprint","IMPRINT",EDGE,{"derivedFrom":sQuery(id+"F0.wireOp",EDGE,"E5.3.4.0")}),1.0]])]});
            var Q36;
            Q36=makeQuery(id+"F0.imprint","IMPRINT",FACE,{"disambiguationData":[TD([[makeQuery(id+"F0.imprint","IMPRINT",EDGE,{"derivedFrom":sQuery(id+"F0.wireOp",EDGE,"E5.4.4.0")}),1.0]])]});
            var Q37;
            Q37=makeQuery(id+"F0.imprint","IMPRINT",FACE,{"disambiguationData":[TD([[makeQuery(id+"F0.imprint","IMPRINT",EDGE,{"derivedFrom":sQuery(id+"F0.wireOp",EDGE,"E5.5.4.0")}),1.0]])]});
            var Q38;
            Q38=makeQuery(id+"F0.imprint","IMPRINT",FACE,{"disambiguationData":[TD([[makeQuery(id+"F0.imprint","IMPRINT",EDGE,{"derivedFrom":sQuery(id+"F0.wireOp",EDGE,"E5.6.4.0")}),1.0]])]});
            var Q39;
            Q39=makeQuery(id+"F0.imprint","IMPRINT",FACE,{"disambiguationData":[TD([[makeQuery(id+"F0.imprint","IMPRINT",EDGE,{"derivedFrom":sQuery(id+"F0.wireOp",EDGE,"E5.7.4.0")}),1.0]])]});
            var Q40;
            Q40=makeQuery(id+"F0.imprint","IMPRINT",FACE,{"disambiguationData":[TD([[makeQuery(id+"F0.imprint","IMPRINT",EDGE,{"derivedFrom":sQuery(id+"F0.wireOp",EDGE,"E5.7.5.0")}),1.0]])]});
            var Q41;
            Q41=makeQuery(id+"F0.imprint","IMPRINT",FACE,{"disambiguationData":[TD([[makeQuery(id+"F0.imprint","IMPRINT",EDGE,{"derivedFrom":sQuery(id+"F0.wireOp",EDGE,"E5.6.5.0")}),1.0]])]});
            var Q42;
            Q42=makeQuery(id+"F0.imprint","IMPRINT",FACE,{"disambiguationData":[TD([[makeQuery(id+"F0.imprint","IMPRINT",EDGE,{"derivedFrom":sQuery(id+"F0.wireOp",EDGE,"E5.5.5.0")}),1.0]])]});
            var Q43;
            Q43=makeQuery(id+"F0.imprint","IMPRINT",FACE,{"disambiguationData":[TD([[makeQuery(id+"F0.imprint","IMPRINT",EDGE,{"derivedFrom":sQuery(id+"F0.wireOp",EDGE,"E5.4.5.0")}),1.0]])]});
            var Q44;
            Q44=makeQuery(id+"F0.imprint","IMPRINT",FACE,{"disambiguationData":[TD([[makeQuery(id+"F0.imprint","IMPRINT",EDGE,{"derivedFrom":sQuery(id+"F0.wireOp",EDGE,"E5.3.5.0")}),1.0]])]});
            var Q45;
            Q45=makeQuery(id+"F0.imprint","IMPRINT",FACE,{"disambiguationData":[TD([[makeQuery(id+"F0.imprint","IMPRINT",EDGE,{"derivedFrom":sQuery(id+"F0.wireOp",EDGE,"E5.2.5.0")}),1.0]])]});
            var Q46;
            Q46=makeQuery(id+"F0.imprint","IMPRINT",FACE,{"disambiguationData":[TD([[makeQuery(id+"F0.imprint","IMPRINT",EDGE,{"derivedFrom":sQuery(id+"F0.wireOp",EDGE,"E5.1.5.0")}),1.0]])]});
            var Q47;
            Q47=makeQuery(id+"F0.imprint","IMPRINT",FACE,{"disambiguationData":[TD([[makeQuery(id+"F0.imprint","IMPRINT",EDGE,{"derivedFrom":sQuery(id+"F0.wireOp",EDGE,"E5.0.5.0")}),1.0]])]});
            var Q48;
            Q48=makeQuery(id+"F0.imprint","IMPRINT",FACE,{"disambiguationData":[TD([[makeQuery(id+"F0.imprint","IMPRINT",EDGE,{"derivedFrom":sQuery(id+"F0.wireOp",EDGE,"E5.0.6.0")}),1.0]])]});
            var Q49;
            Q49=makeQuery(id+"F0.imprint","IMPRINT",FACE,{"disambiguationData":[TD([[makeQuery(id+"F0.imprint","IMPRINT",EDGE,{"derivedFrom":sQuery(id+"F0.wireOp",EDGE,"E5.1.6.0")}),1.0]])]});
            var Q50;
            Q50=makeQuery(id+"F0.imprint","IMPRINT",FACE,{"disambiguationData":[TD([[makeQuery(id+"F0.imprint","IMPRINT",EDGE,{"derivedFrom":sQuery(id+"F0.wireOp",EDGE,"E5.2.6.0")}),1.0]])]});
            var Q51;
            Q51=makeQuery(id+"F0.imprint","IMPRINT",FACE,{"disambiguationData":[TD([[makeQuery(id+"F0.imprint","IMPRINT",EDGE,{"derivedFrom":sQuery(id+"F0.wireOp",EDGE,"E5.3.6.0")}),1.0]])]});
            var Q52;
            Q52=makeQuery(id+"F0.imprint","IMPRINT",FACE,{"disambiguationData":[TD([[makeQuery(id+"F0.imprint","IMPRINT",EDGE,{"derivedFrom":sQuery(id+"F0.wireOp",EDGE,"E5.4.6.0")}),1.0]])]});
            var Q53;
            Q53=makeQuery(id+"F0.imprint","IMPRINT",FACE,{"disambiguationData":[TD([[makeQuery(id+"F0.imprint","IMPRINT",EDGE,{"derivedFrom":sQuery(id+"F0.wireOp",EDGE,"E5.5.6.0")}),1.0]])]});
            var Q54;
            Q54=makeQuery(id+"F0.imprint","IMPRINT",FACE,{"disambiguationData":[TD([[makeQuery(id+"F0.imprint","IMPRINT",EDGE,{"derivedFrom":sQuery(id+"F0.wireOp",EDGE,"E5.6.6.0")}),1.0]])]});
            var Q55;
            Q55=makeQuery(id+"F0.imprint","IMPRINT",FACE,{"disambiguationData":[TD([[makeQuery(id+"F0.imprint","IMPRINT",EDGE,{"derivedFrom":sQuery(id+"F0.wireOp",EDGE,"E5.7.6.0")}),1.0]])]});
            var Q56;
            Q56=makeQuery(id+"F0.imprint","IMPRINT",FACE,{"disambiguationData":[TD([[makeQuery(id+"F0.imprint","IMPRINT",EDGE,{"derivedFrom":sQuery(id+"F0.wireOp",EDGE,"E5.7.7.0")}),1.0]])]});
            var Q57;
            Q57=makeQuery(id+"F0.imprint","IMPRINT",FACE,{"disambiguationData":[TD([[makeQuery(id+"F0.imprint","IMPRINT",EDGE,{"derivedFrom":sQuery(id+"F0.wireOp",EDGE,"E5.6.7.0")}),1.0]])]});
            var Q58;
            Q58=makeQuery(id+"F0.imprint","IMPRINT",FACE,{"disambiguationData":[TD([[makeQuery(id+"F0.imprint","IMPRINT",EDGE,{"derivedFrom":sQuery(id+"F0.wireOp",EDGE,"E5.5.7.0")}),1.0]])]});
            var Q59;
            Q59=makeQuery(id+"F0.imprint","IMPRINT",FACE,{"disambiguationData":[TD([[makeQuery(id+"F0.imprint","IMPRINT",EDGE,{"derivedFrom":sQuery(id+"F0.wireOp",EDGE,"E5.4.7.0")}),1.0]])]});
            var Q60;
            Q60=makeQuery(id+"F0.imprint","IMPRINT",FACE,{"disambiguationData":[TD([[makeQuery(id+"F0.imprint","IMPRINT",EDGE,{"derivedFrom":sQuery(id+"F0.wireOp",EDGE,"E5.3.7.0")}),1.0]])]});
            var Q61;
            Q61=makeQuery(id+"F0.imprint","IMPRINT",FACE,{"disambiguationData":[TD([[makeQuery(id+"F0.imprint","IMPRINT",EDGE,{"derivedFrom":sQuery(id+"F0.wireOp",EDGE,"E5.2.7.0")}),1.0]])]});
            var Q62;
            Q62=makeQuery(id+"F0.imprint","IMPRINT",FACE,{"disambiguationData":[TD([[makeQuery(id+"F0.imprint","IMPRINT",EDGE,{"derivedFrom":sQuery(id+"F0.wireOp",EDGE,"E5.0.7.0")}),1.0]])]});
            var Q63;
            Q63=makeQuery(id+"F0.imprint","IMPRINT",FACE,{"disambiguationData":[TD([[makeQuery(id+"F0.imprint","IMPRINT",EDGE,{"derivedFrom":sQuery(id+"F0.wireOp",EDGE,"E5.1.7.0")}),1.0]])]});
            extrude(context, id + "F2", {"entities" : qUnion([Q0, Q1, Q2, Q3, Q4, Q5, Q6, Q7, Q8, Q9, Q10, Q11, Q12, Q13, Q14, Q15, Q16, Q17, Q18, Q19, Q20, Q21, Q22, Q23, Q24, Q25, Q26, Q27, Q28, Q29, Q30, Q31, Q32, Q33, Q34, Q35, Q36, Q37, Q38, Q39, Q40, Q41, Q42, Q43, Q44, Q45, Q46, Q47, Q48, Q49, Q50, Q51, Q52, Q53, Q54, Q55, Q56, Q57, Q58, Q59, Q60, Q61, Q62, Q63]), "operationType" : NewBodyOperationType.REMOVE, "oppositeDirection" : true, "depth" : 2 * mm});
        }
    });
